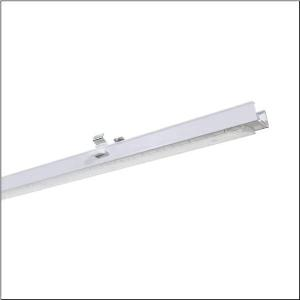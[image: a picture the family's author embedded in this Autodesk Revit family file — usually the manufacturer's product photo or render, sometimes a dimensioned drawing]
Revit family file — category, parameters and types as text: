
# Revit family: trunking_flex_31_51re11mb48b
name_source: partatom
category: Lighting Fixtures
units: mm (PartAtom-declared; Revit-internal decimal feet)

## family parameters
Cut with Voids When Loaded = No
Host = Face
Light Source = No
Part Type = Normal
Room Calculation Point = No
Round Connector Dimension = Use Diameter
Shared = No

## types (1)
- --- (1 x LED, 8000 lm, 50 W, 4000K)
    Apparent Load = 50 VA
    CIE Flux Codes = 83 93 98 100 100
    Color Rendering = 80
    Color Temperature = 4000K
    Default Elevation = 1800 mm
    Description = Trunking Flex 31, luminaire insert, of extruded aluminium section, coated, traffic white (RAL 9016), length: 1.472mm, width: 91mm, height: 53mm, LED rated luminous flux: 8.000lm, light colour: 840, control gear: ON/OFF Multilumen, with system connector: socket, mains connection: 220..240V, AC, 50/60Hz, rated input power: 50W, luminous flux adjustable on luminaire in four steps (4130/5610/6850/8000lm), connected load according to luminous flux setting (25/34/42/50W), primary light control with lens, of plastic, primary optical cover: cover, of PMMA, light emission: direct distribution, protection rating (complete): IP20, insulation class (complete): insulation class I (protective earthing), certification: CE, UKCA, impact resistance: IK02, permissible ambient temperature for indoor applications: -20..+40°C, packaging unit: 1 piece
    Height = 58 mm
    Lamp = 1 x LED
    Lamp Light Flux = 8000 lm
    Lamp Power = 50 W
    Lamp count = 1
    Length = 1472 mm
    Luminous efficacy = 160 lm/W
    Manufacturer = Siteco
    ModVariant = No
    Model = 51RE11MB48B
    Mounting Place = Ceiling
    Mounting Type = Pendant
    Number of Poles = 1
    OnlyDefault = Yes
    Power Factor = 1
    Product Name = Trunking Flex 31
    Product group = luminaire insert
    ProductGroupID = 901
    Protection Class = Protection class I
    Protection Degree = IP 20
    RLX_Detail_Level = 1
    RLX_Emergency_Light_Flux = 0 lm
    RLX_Emergency_Type = 0
    RLX_Emergency_Type_DB = No
    RlxData = <blob elided: 20217 chars, md5=8da60f2a>
    Socket = socket
    Standby Power = 0 W
    System Light Flux = 8000 lm
    System Power = 50 W
    Type Comments = factory setting: luminous flux: 100 % | (ON | ON) | 300 mA
    Type Image = l_1266702.jpg
    URL = http://relux.com
    VarID = @adj_001407
    Voltage = 0 V
    Weight = 0.00 kg
    Width = 65 mm

## geometry (parser evidence)
native form markers: Blend x4, Sweep x9
no freeform markers — native parametric forms only
